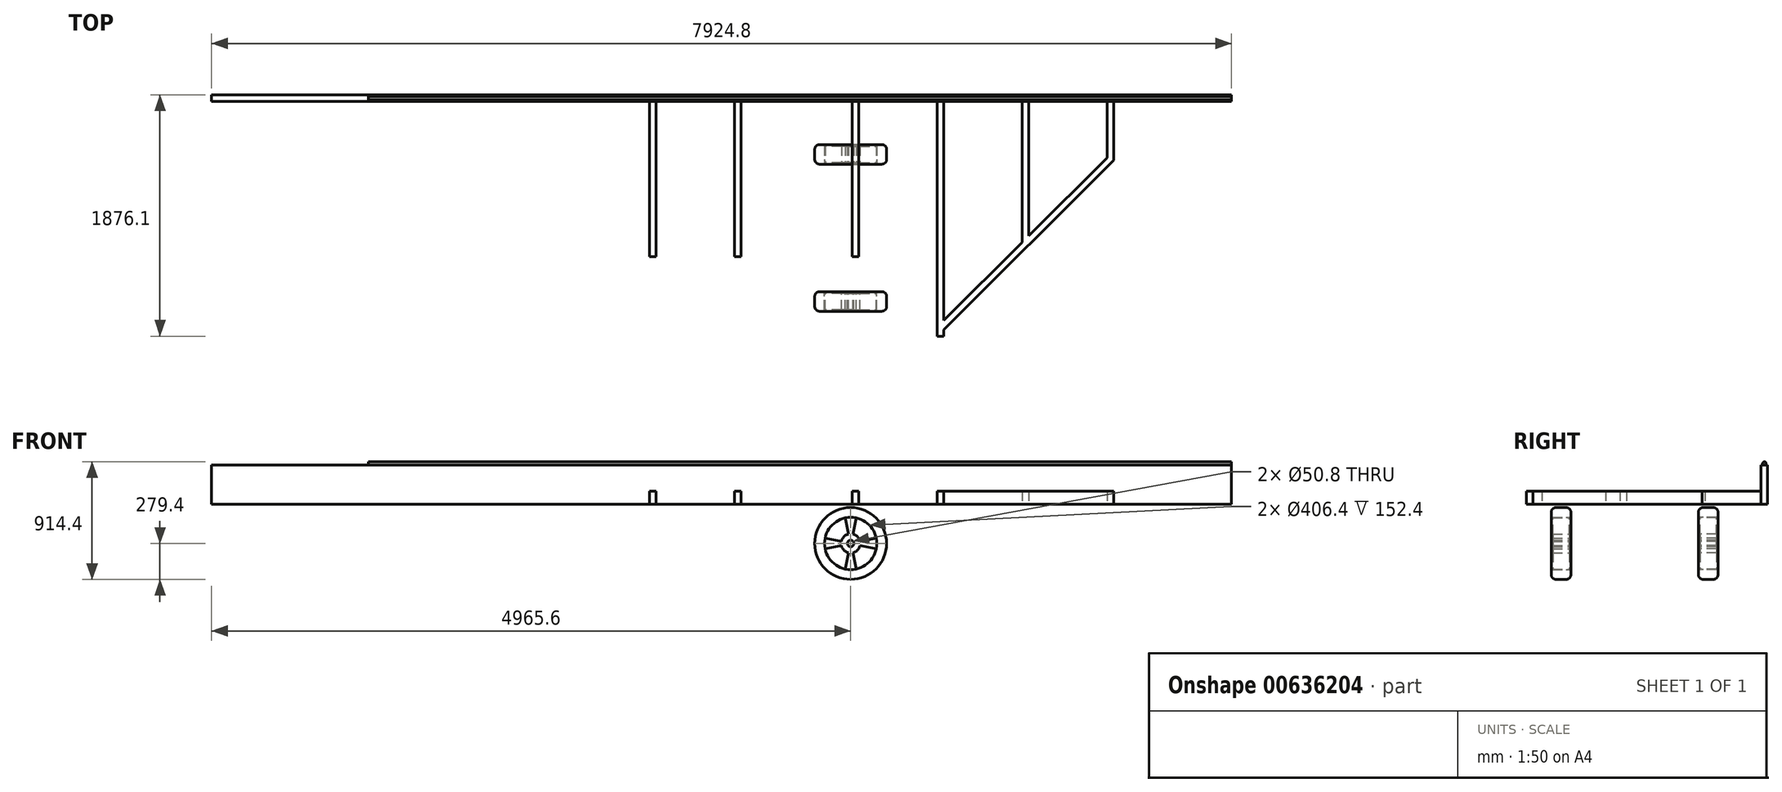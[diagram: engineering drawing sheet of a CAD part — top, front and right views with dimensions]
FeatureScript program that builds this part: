
annotation { "Feature Type Name" : "Feature", "Feature Type Description" : "" }
export const myFeature = defineFeature(function(context is Context, id is Id, definition is map)
    precondition{}
    {
        {
            var Q0;
            Q0=qCreatedBy(makeId("Top.planeOp"),FACE);
            var sketch = newSketch(context, id + "F0", { "sketchPlane" : qUnion([Q0])});
            skLineSegment(sketch, "E0.bottom", {"start": v(-4964.89, 1033.97) * mm, "end": v(2959.91, 1033.97) * mm});
            skLineSegment(sketch, "E0.right", {"start": v(2959.91, 1033.97) * mm, "end": v(2959.91, 983.17) * mm});
            skLineSegment(sketch, "E1.0", {"start": v(-4964.89, 983.17) * mm, "end": v(-3898.09, 983.17) * mm});
            skLineSegment(sketch, "E2", {"start": v(1994.71, 983.17) * mm, "end": v(2959.91, 983.17) * mm});
            skLineSegment(sketch, "E3.bottom", {"start": v(-3898.09, 983.17) * mm, "end": v(-3491.69, 983.17) * mm});
            skLineSegment(sketch, "E3.top", {"start": v(-3898.09, 68.77) * mm, "end": v(-3491.69, 68.77) * mm});
            skLineSegment(sketch, "E3.left", {"start": v(-3898.09, 983.17) * mm, "end": v(-3898.09, 68.77) * mm});
            skLineSegment(sketch, "E3.right", {"start": v(-3491.69, 983.17) * mm, "end": v(-3491.69, 68.77) * mm});
            skLineSegment(sketch, "E4.bottom", {"start": v(-4660.09, 983.17) * mm, "end": v(-4202.89, 983.17) * mm});
            skLineSegment(sketch, "E4.top", {"start": v(-4660.09, 678.37) * mm, "end": v(-4202.89, 678.37) * mm});
            skLineSegment(sketch, "E4.left", {"start": v(-4660.09, 983.17) * mm, "end": v(-4660.09, 678.37) * mm});
            skLineSegment(sketch, "E4.right", {"start": v(-4202.89, 983.17) * mm, "end": v(-4202.89, 678.37) * mm});
            skLineSegment(sketch, "E5.bottom", {"start": v(-5245.26, 798.14) * mm, "end": v(-5066.49, 798.14) * mm});
            skLineSegment(sketch, "E5.top", {"start": v(-5245.26, 487.61) * mm, "end": v(-5066.49, 487.61) * mm});
            skLineSegment(sketch, "E5.left", {"start": v(-5245.26, 798.14) * mm, "end": v(-5245.26, 487.61) * mm});
            skLineSegment(sketch, "E5.right", {"start": v(-5066.49, 798.14) * mm, "end": v(-5066.49, 487.61) * mm});
            skLineSegment(sketch, "E6", {"start": v(673.91, 983.17) * mm, "end": v(673.91, -842.13) * mm});
            skLineSegment(sketch, "E7", {"start": v(64.31, 983.17) * mm, "end": v(64.31, -224.16) * mm});
            skLineSegment(sketch, "E8.0", {"start": v(724.71, 983.17) * mm, "end": v(724.71, -842.13) * mm});
            skLineSegment(sketch, "E9.0", {"start": v(13.51, 983.17) * mm, "end": v(13.51, -224.16) * mm});
            skLineSegment(sketch, "E10.trimOffspring", {"start": v(724.71, 983.17) * mm, "end": v(1994.71, 983.17) * mm});
            skLineSegment(sketch, "E11.trimOffspring", {"start": v(64.31, 983.17) * mm, "end": v(673.91, 983.17) * mm});
            skLineSegment(sketch, "E12", {"start": v(-900.89, 983.17) * mm, "end": v(-900.89, -224.16) * mm});
            skLineSegment(sketch, "E13", {"start": v(-1510.49, 983.17) * mm, "end": v(-1510.49, -224.16) * mm});
            skLineSegment(sketch, "E14.0", {"start": v(-1561.29, 983.17) * mm, "end": v(-1561.29, -224.16) * mm});
            skLineSegment(sketch, "E15.0", {"start": v(-850.09, 983.17) * mm, "end": v(-850.09, -224.16) * mm});
            skLineSegment(sketch, "E16.trimOffspring", {"start": v(-1510.49, 983.17) * mm, "end": v(-900.89, 983.17) * mm});
            skLineSegment(sketch, "E17.trimOffspring", {"start": v(-850.09, 983.17) * mm, "end": v(13.51, 983.17) * mm});
            skLineSegment(sketch, "E18.bottom", {"start": v(-3381.65, 1374.5) * mm, "end": v(1469.4, 1374.5) * mm});
            skLineSegment(sketch, "E18.top", {"start": v(-3381.65, 1104.9) * mm, "end": v(1469.4, 1104.9) * mm});
            skLineSegment(sketch, "E18.left", {"start": v(-3381.65, 1374.5) * mm, "end": v(-3381.65, 1104.9) * mm});
            skLineSegment(sketch, "E18.right", {"start": v(1469.4, 1374.5) * mm, "end": v(1469.4, 1104.9) * mm});
            skText(sketch, "E19", { "text": "Sawdust", "fontName": "OpenSans-Bold.ttf"});
            skLineSegment(sketch, "E20", {"start": v(13.51, 983.17) * mm, "end": v(64.31, 983.17) * mm});
            skLineSegment(sketch, "E21", {"start": v(13.51, -224.16) * mm, "end": v(64.31, -224.16) * mm});
            skLineSegment(sketch, "E22", {"start": v(673.91, 983.17) * mm, "end": v(724.71, 983.17) * mm});
            skLineSegment(sketch, "E23.trimOffspring", {"start": v(-3491.69, 983.17) * mm, "end": v(-1561.29, 983.17) * mm});
            skLineSegment(sketch, "E24", {"start": v(-900.89, 983.17) * mm, "end": v(-850.09, 983.17) * mm});
            skLineSegment(sketch, "E25", {"start": v(-1561.29, 983.17) * mm, "end": v(-1510.49, 983.17) * mm});
            skPoint(sketch, "E26", {"position": v(-877.9, 2951.3) * mm});
            skPoint(sketch, "E27.start.orphan", {"position": v(-3898.09, 983.17) * mm});
            skPoint(sketch, "E28.0.start.orphan", {"position": v(2045.51, 983.17) * mm});
            skLineSegment(sketch, "E29", {"start": v(2045.51, 983.17) * mm, "end": v(2045.51, 524.26) * mm});
            skLineSegment(sketch, "E30", {"start": v(2045.51, 524.26) * mm, "end": v(724.71, -790.95) * mm});
            skLineSegment(sketch, "E31", {"start": v(673.91, -842.13) * mm, "end": v(724.71, -842.13) * mm});
            skLineSegment(sketch, "E32.0", {"start": v(1994.71, 545.36) * mm, "end": v(724.71, -719.26) * mm});
            skLineSegment(sketch, "E32.1", {"start": v(1994.71, 983.17) * mm, "end": v(1994.71, 545.36) * mm});
            skLineSegment(sketch, "E33", {"start": v(1334.31, 983.17) * mm, "end": v(1334.31, -112.24) * mm});
            skLineSegment(sketch, "E34", {"start": v(1385.11, 983.17) * mm, "end": v(1385.11, -61.66) * mm});
            skLineSegment(sketch, "E35", {"start": v(1468.62, 983.17) * mm, "end": v(1468.62, 906.97) * mm});
            skLineSegment(sketch, "E36", {"start": v(1468.62, 906.97) * mm, "end": v(1544.82, 906.97) * mm});
            skLineSegment(sketch, "E37", {"start": v(1544.82, 906.97) * mm, "end": v(1544.82, 983.17) * mm});
            skLineSegment(sketch, "E38", {"start": v(-4964.89, 983.17) * mm, "end": v(-4964.89, 1033.97) * mm});
            skLineSegment(sketch, "E39", {"start": v(-1561.29, -224.16) * mm, "end": v(-1510.49, -224.16) * mm});
            skLineSegment(sketch, "E40", {"start": v(-900.89, -224.16) * mm, "end": v(-850.09, -224.16) * mm});
            const initialGuessF0  = {"E19": [-1.35786, 1.1049, 1, 0, 0.254]};
            skSetInitialGuess(sketch, initialGuessF0);
            skSolve(sketch);
        }
        {
            var Q0;
            {var subQ9=sQuery(id+"F0.wireOp",EDGE,"E0.bottom");Q0=makeQuery(id+"F0.imprint","IMPRINT",FACE,{"disambiguationData":[TD([[makeQuery(id+"F0.imprint","IMPRINT",EDGE,{"derivedFrom":subQ9}),-1.0]])]});}
            extrude(context, id + "F1", {"entities" : qUnion([Q0]), "depth" : 304.8 * mm, "offsetDistance" : 25.4 * mm});
        }
        {
            var Q0;
            {var subQ1=sQuery(id+"F0.wireOp",EDGE,"E29");Q0=makeQuery(id+"F0.imprint","IMPRINT",FACE,{"disambiguationData":[TD([[makeQuery(id+"F0.imprint","IMPRINT",EDGE,{"derivedFrom":subQ1}),-1.0]])]});}
            var Q1;
            {var subQ0=sQuery(id+"F0.wireOp",EDGE,"E33");Q1=makeQuery(id+"F0.imprint","IMPRINT",FACE,{"disambiguationData":[TD([[makeQuery(id+"F0.imprint","IMPRINT",EDGE,{"derivedFrom":subQ0}),1.0]])]});}
            var Q2;
            Q2=makeQuery(id+"F0.imprint","IMPRINT",FACE,{"disambiguationData":[TD([[makeQuery(id+"F0.imprint","IMPRINT",EDGE,{"derivedFrom":sQuery(id+"F0.wireOp",EDGE,"E6")}),1.0]])]});
            var Q3;
            Q3=makeQuery(id+"F0.imprint","IMPRINT",FACE,{"disambiguationData":[TD([[makeQuery(id+"F0.imprint","IMPRINT",EDGE,{"derivedFrom":sQuery(id+"F0.wireOp",EDGE,"E7")}),-1.0]])]});
            var Q4;
            Q4=makeQuery(id+"F0.imprint","IMPRINT",FACE,{"disambiguationData":[TD([[makeQuery(id+"F0.imprint","IMPRINT",EDGE,{"derivedFrom":sQuery(id+"F0.wireOp",EDGE,"E12")}),1.0]])]});
            var Q5;
            Q5=makeQuery(id+"F0.imprint","IMPRINT",FACE,{"disambiguationData":[TD([[makeQuery(id+"F0.imprint","IMPRINT",EDGE,{"derivedFrom":sQuery(id+"F0.wireOp",EDGE,"E13")}),-1.0]])]});
            extrude(context, id + "F2", {"entities" : qUnion([Q0, Q1, Q2, Q3, Q4, Q5]), "operationType" : NewBodyOperationType.ADD, "depth" : 101.6 * mm, "offsetDistance" : 25.4 * mm});
        }
        {
            var Q0;
            Q0=makeQuery(id+"F1.opExtrude","SWEPT_FACE",FACE,{"disambiguationData":[OSD([sQuery(id+"F0.wireOp",EDGE,"E0.right")])]});
            var sketch = newSketch(context, id + "F3", { "sketchPlane" : qUnion([Q0])});
            skCircle(sketch, "E41", {"center": v(1008.57, 317.5) * mm, "radius": 12.7 * mm});
            skPoint(sketch, "E41.centerSnap0", {"position": v(1008.57, 304.8) * mm});
            skSolve(sketch);
        }
        {
            var Q0;
            Q0 = qSketchRegion(id + "F3", true);
            extrude(context, id + "F4", {"entities" : qUnion([Q0]), "operationType" : NewBodyOperationType.ADD, "oppositeDirection" : true, "depth" : 6705.6 * mm, "offsetDistance" : 25.4 * mm});
        }
        {
            var Q0;
            Q0=qCreatedBy(makeId("Front.planeOp"),FACE);
            cPlane(context, id + "F5", {"entities" : qUnion([Q0]), "cplaneType" : CPlaneType.OFFSET, "offset" : 571.5 * mm, "width" : 152.4 * mm, "height" : 152.4 * mm});
        }
        {
            var Q0;
            Q0=qCreatedBy(id+"F5.planeOp",FACE);
            var sketch = newSketch(context, id + "F6", { "sketchPlane" : qUnion([Q0])});
            skCircle(sketch, "E42", {"center": v(0.72, -304.8) * mm, "radius": 203.2 * mm});
            skCircle(sketch, "E43", {"center": v(0.72, -304.8) * mm, "radius": 279.4 * mm});
            skCircle(sketch, "E44", {"center": v(0.72, -304.8) * mm, "radius": 74.22 * mm});
            skLineSegment(sketch, "E45", {"start": v(0.72, 925.44) * mm, "end": v(0.72, -945.96) * mm, "construction": true});
            skLineSegment(sketch, "E46", {"start": v(-15.94, -232.48) * mm, "end": v(-41.53, -106.04) * mm});
            skLineSegment(sketch, "E47.MirrorCS", {"start": v(17.37, -232.48) * mm, "end": v(42.96, -106.04) * mm});
            skLineSegment(sketch, "E48.1.0", {"start": v(-71.6, -321.46) * mm, "end": v(-198.04, -347.05) * mm});
            skLineSegment(sketch, "E48.1.1", {"start": v(-71.6, -288.14) * mm, "end": v(-198.04, -262.55) * mm});
            skLineSegment(sketch, "E48.2.0", {"start": v(17.37, -377.12) * mm, "end": v(42.96, -503.56) * mm});
            skLineSegment(sketch, "E48.2.1", {"start": v(-15.94, -377.12) * mm, "end": v(-41.53, -503.56) * mm});
            skLineSegment(sketch, "E48.3.0", {"start": v(73.04, -288.14) * mm, "end": v(199.48, -262.55) * mm});
            skLineSegment(sketch, "E48.3.1", {"start": v(73.04, -321.46) * mm, "end": v(199.48, -347.05) * mm});
            skCircle(sketch, "E49", {"center": v(0.72, -304.8) * mm, "radius": 25.4 * mm});
            skSolve(sketch);
        }
        {
            var Q0;
            Q0=makeQuery(id+"F6.imprint","IMPRINT",FACE,{"disambiguationData":[TD([[makeQuery(id+"F6.imprint","IMPRINT",EDGE,{"derivedFrom":sQuery(id+"F6.wireOp",EDGE,"E43")}),1.0]])]});
            extrude(context, id + "F7", {"entities" : qUnion([Q0]), "endBound" : BoundingType.SYMMETRIC, "depth" : 152.4 * mm, "offsetDistance" : 25.4 * mm});
        }
        {
            var Q0;
            Q0=makeQuery(id+"F7.opExtrude","CAP_EDGE",EDGE,{"disambiguationData":[OSD([sQuery(id+"F6.wireOp",EDGE,"E43")])],"isStart":false});
            var Q1;
            Q1=makeQuery(id+"F7.opExtrude","CAP_EDGE",EDGE,{"disambiguationData":[OSD([sQuery(id+"F6.wireOp",EDGE,"E43")])],"isStart":true});
            fillet(context, id + "F8", {"entities" : qUnion([Q0, Q1]), "radius" : 36.8 * mm, "tangentPropagation" : true, "allowEdgeOverflow" : false});
        }
        {
            var Q0;
            {var subQ0=sQuery(id+"F6.wireOp",EDGE,"E46");Q0=makeQuery(id+"F6.imprint","IMPRINT",FACE,{"disambiguationData":[TD([[makeQuery(id+"F6.imprint","IMPRINT",EDGE,{"derivedFrom":subQ0}),-1.0]])]});}
            var Q1;
            {var subQ0=sQuery(id+"F6.wireOp",EDGE,"E48.3.0");Q1=makeQuery(id+"F6.imprint","IMPRINT",FACE,{"disambiguationData":[TD([[makeQuery(id+"F6.imprint","IMPRINT",EDGE,{"derivedFrom":subQ0}),-1.0]])]});}
            var Q2;
            {var subQ0=sQuery(id+"F6.wireOp",EDGE,"E48.1.0");Q2=makeQuery(id+"F6.imprint","IMPRINT",FACE,{"disambiguationData":[TD([[makeQuery(id+"F6.imprint","IMPRINT",EDGE,{"derivedFrom":subQ0}),-1.0]])]});}
            var Q3;
            {var subQ0=sQuery(id+"F6.wireOp",EDGE,"E48.2.0");Q3=makeQuery(id+"F6.imprint","IMPRINT",FACE,{"disambiguationData":[TD([[makeQuery(id+"F6.imprint","IMPRINT",EDGE,{"derivedFrom":subQ0}),-1.0]])]});}
            var Q4;
            {var subQ0=sQuery(id+"F6.wireOp",EDGE,"E44");var subQ4=makeQuery(id+"F6.imprint","INTERSECT",VERTEX,{"derivedFrom":[subQ0,sQuery(id+"F6.wireOp",EDGE,"E47.MirrorCS")]});Q4=makeQuery(id+"F6.imprint","IMPRINT",FACE,{"disambiguationData":[TD([[makeQuery(id+"F6.imprint","IMPRINT",EDGE,{"disambiguationData":[TD([[subQ4,1.0]])],"derivedFrom":subQ0}),1.0]])]});}
            extrude(context, id + "F9", {"entities" : qUnion([Q0, Q1, Q2, Q3, Q4]), "endBound" : BoundingType.SYMMETRIC, "depth" : 127 * mm, "offsetDistance" : 25.4 * mm});
        }
        {
            var Q0;
            Q0=makeQuery(id+"F9.opExtrude","SWEPT_BODY",BODY,{"disambiguationData":[OSD([sQuery(id+"F6.wireOp",EDGE,"E42"),sQuery(id+"F6.wireOp",EDGE,"E44"),sQuery(id+"F6.wireOp",EDGE,"E46"),sQuery(id+"F6.wireOp",EDGE,"E47.MirrorCS"),sQuery(id+"F6.wireOp",EDGE,"E48.1.0"),sQuery(id+"F6.wireOp",EDGE,"E48.1.1"),sQuery(id+"F6.wireOp",EDGE,"E48.2.0"),sQuery(id+"F6.wireOp",EDGE,"E48.2.1"),sQuery(id+"F6.wireOp",EDGE,"E48.3.0"),sQuery(id+"F6.wireOp",EDGE,"E48.3.1"),sQuery(id+"F6.wireOp",EDGE,"E49")])]});
            var Q1;
            Q1=makeQuery(id+"F7.opExtrude","SWEPT_BODY",BODY,{"disambiguationData":[OSD([sQuery(id+"F6.wireOp",EDGE,"E42"),sQuery(id+"F6.wireOp",EDGE,"E43")])]});
            var Q2;
            Q2=qCreatedBy(makeId("Front.planeOp"),FACE);
            mirror(context, id + "F10", {"entities" : qUnion([Q0, Q1]), "mirrorPlane" : qUnion([Q2])});
        }
    });
